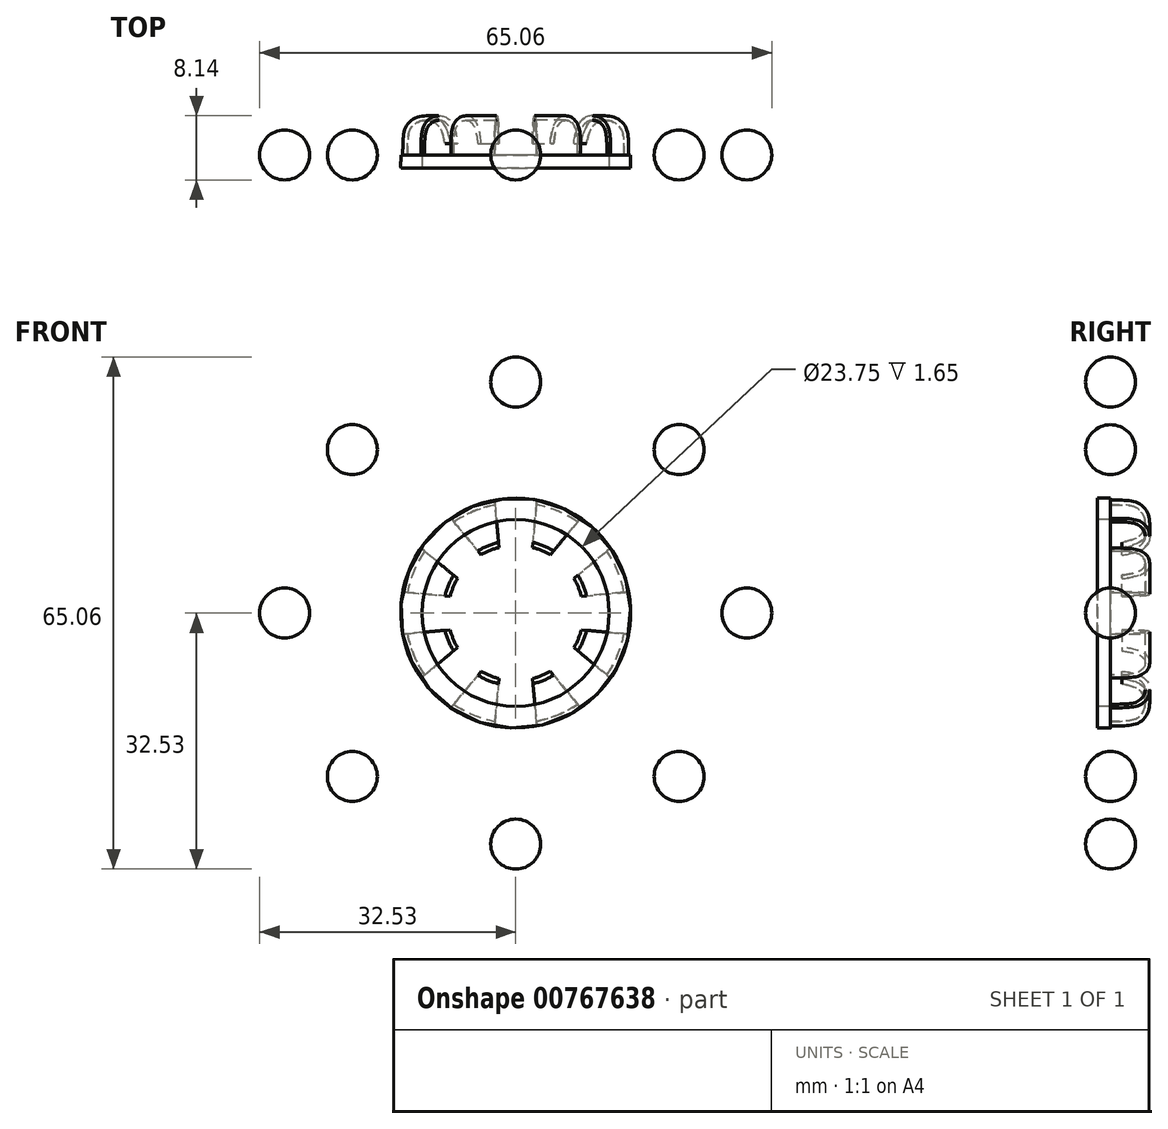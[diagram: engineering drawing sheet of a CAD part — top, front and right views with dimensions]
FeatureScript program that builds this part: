
annotation { "Feature Type Name" : "Feature", "Feature Type Description" : "" }
export const myFeature = defineFeature(function(context is Context, id is Id, definition is map)
    precondition{}
    {
        {
            var Q0;
            Q0=qCreatedBy(makeId("Front.planeOp"),FACE);
            var sketch = newSketch(context, id + "F0", { "sketchPlane" : qUnion([Q0])});
            skCircle(sketch, "E0", {"center": v(0, 0) * mm, "radius": 14.6 * mm});
            skCircle(sketch, "E1", {"center": v(0, 0) * mm, "radius": 11.88 * mm});
            skSolve(sketch);
        }
        {
            var Q0;
            Q0=qCreatedBy(makeId("Front.planeOp"),FACE);
            var sketch = newSketch(context, id + "F1", { "sketchPlane" : qUnion([Q0])});
            skLineSegment(sketch, "E2", {"start": v(0, 0) * mm, "end": v(-49.04, 0) * mm});
            skLineSegment(sketch, "E3", {"start": v(0, 0) * mm, "end": v(-28.37, 28.37) * mm});
            skLineSegment(sketch, "E4", {"start": v(-28.37, 28.37) * mm, "end": v(0, 0) * mm});
            skLineSegment(sketch, "E5", {"start": v(0, 0) * mm, "end": v(0, 0) * mm});
            skLineSegment(sketch, "E6", {"start": v(0, 0) * mm, "end": v(31.83, 31.83) * mm});
            skLineSegment(sketch, "E7", {"start": v(31.83, 31.83) * mm, "end": v(0, 0) * mm});
            skLineSegment(sketch, "E8", {"start": v(0, 0) * mm, "end": v(55.32, 0) * mm});
            skLineSegment(sketch, "E9.MirrorCS", {"start": v(-28.37, -28.37) * mm, "end": v(0, 0) * mm});
            skLineSegment(sketch, "E10.MirrorCS", {"start": v(31.83, -31.83) * mm, "end": v(0, 0) * mm});
            skLineSegment(sketch, "E11", {"start": v(0, 0) * mm, "end": v(0, -25.11) * mm});
            skLineSegment(sketch, "E12", {"start": v(0, -25.11) * mm, "end": v(0, 0) * mm});
            skLineSegment(sketch, "E13", {"start": v(0, 0) * mm, "end": v(-9.1, -21.98) * mm});
            skLineSegment(sketch, "E14", {"start": v(5.91, -1.9) * mm, "end": v(5.91, 1.9) * mm});
            skLineSegment(sketch, "E15", {"start": v(14.8, 2.73) * mm, "end": v(5.91, 1.9) * mm});
            skLineSegment(sketch, "E16", {"start": v(5.91, -1.9) * mm, "end": v(14.8, -2.72) * mm});
            skLineSegment(sketch, "E17", {"start": v(14.8, 2.73) * mm, "end": v(14.8, -2.72) * mm});
            skLineSegment(sketch, "E18.MirrorCS", {"start": v(2.72, 14.8) * mm, "end": v(1.9, 5.91) * mm});
            skLineSegment(sketch, "E19.MirrorCS", {"start": v(-1.9, 5.91) * mm, "end": v(-2.73, 14.8) * mm});
            skLineSegment(sketch, "E20.MirrorCS", {"start": v(2.72, 14.8) * mm, "end": v(-2.73, 14.8) * mm});
            skLineSegment(sketch, "E21.MirrorCS", {"start": v(-1.9, 5.91) * mm, "end": v(1.9, 5.91) * mm});
            skLineSegment(sketch, "E22.MirrorCS", {"start": v(-2.73, -14.8) * mm, "end": v(2.72, -14.8) * mm});
            skLineSegment(sketch, "E23.MirrorCS", {"start": v(-2.73, -14.8) * mm, "end": v(-1.9, -5.91) * mm});
            skLineSegment(sketch, "E24.MirrorCS", {"start": v(1.9, -5.91) * mm, "end": v(-1.9, -5.91) * mm});
            skLineSegment(sketch, "E25.MirrorCS", {"start": v(1.9, -5.91) * mm, "end": v(2.72, -14.8) * mm});
            skLineSegment(sketch, "E26.MirrorCS", {"start": v(-5.91, -1.9) * mm, "end": v(-5.91, 1.9) * mm});
            skLineSegment(sketch, "E27.MirrorCS", {"start": v(-14.8, 2.73) * mm, "end": v(-5.91, 1.9) * mm});
            skLineSegment(sketch, "E28.MirrorCS", {"start": v(-14.8, 2.73) * mm, "end": v(-14.8, -2.72) * mm});
            skLineSegment(sketch, "E29.MirrorCS", {"start": v(-5.91, -1.9) * mm, "end": v(-14.8, -2.72) * mm});
            skLineSegment(sketch, "E30.MirrorCS", {"start": v(-8.54, -12.4) * mm, "end": v(-2.84, -5.53) * mm});
            skLineSegment(sketch, "E31.MirrorCS", {"start": v(-5.53, -2.84) * mm, "end": v(-2.84, -5.53) * mm});
            skLineSegment(sketch, "E32.MirrorCS", {"start": v(-5.53, -2.84) * mm, "end": v(-12.4, -8.54) * mm});
            skLineSegment(sketch, "E33.MirrorCS", {"start": v(-8.54, -12.4) * mm, "end": v(-12.4, -8.54) * mm});
            skLineSegment(sketch, "E34.MirrorCS", {"start": v(2.84, 5.53) * mm, "end": v(5.53, 2.84) * mm});
            skLineSegment(sketch, "E35.MirrorCS", {"start": v(2.84, 5.53) * mm, "end": v(8.54, 12.4) * mm});
            skLineSegment(sketch, "E36.MirrorCS", {"start": v(12.4, 8.54) * mm, "end": v(5.53, 2.84) * mm});
            skLineSegment(sketch, "E37.MirrorCS", {"start": v(12.4, 8.54) * mm, "end": v(8.54, 12.4) * mm});
            skLineSegment(sketch, "E38.MirrorCS", {"start": v(-5.53, 2.84) * mm, "end": v(-2.84, 5.53) * mm});
            skLineSegment(sketch, "E39.MirrorCS", {"start": v(-8.54, 12.4) * mm, "end": v(-2.84, 5.53) * mm});
            skLineSegment(sketch, "E40.MirrorCS", {"start": v(-8.54, 12.4) * mm, "end": v(-12.4, 8.54) * mm});
            skLineSegment(sketch, "E41.MirrorCS", {"start": v(-5.53, 2.84) * mm, "end": v(-12.4, 8.54) * mm});
            skLineSegment(sketch, "E42.MirrorCS", {"start": v(-1.9, -5.91) * mm, "end": v(1.9, -5.91) * mm});
            skLineSegment(sketch, "E43.MirrorCS", {"start": v(-1.9, -5.91) * mm, "end": v(-2.72, -14.8) * mm});
            skLineSegment(sketch, "E44.MirrorCS", {"start": v(2.73, -14.8) * mm, "end": v(-2.72, -14.8) * mm});
            skLineSegment(sketch, "E45.MirrorCS", {"start": v(5.53, -2.84) * mm, "end": v(2.84, -5.53) * mm});
            skLineSegment(sketch, "E46.MirrorCS", {"start": v(5.53, -2.84) * mm, "end": v(12.4, -8.54) * mm});
            skLineSegment(sketch, "E47.MirrorCS", {"start": v(8.54, -12.4) * mm, "end": v(12.4, -8.54) * mm});
            skLineSegment(sketch, "E48.MirrorCS", {"start": v(8.54, -12.4) * mm, "end": v(2.84, -5.53) * mm});
            skSolve(sketch);
        }
        {
            var Q0;
            Q0=qCreatedBy(makeId("Top.planeOp"),FACE);
            var sketch = newSketch(context, id + "F2", { "sketchPlane" : qUnion([Q0])});
            skFitSpline(sketch, "E49", {"points": [v(-14.6, 0) * mm, v(-14.44, 2.84) * mm, v(-13.73, 4.2) * mm, v(-11.98, 4.95) * mm, v(-9.72, 4.28) * mm, v(-8.73, 2.27) * mm, v(-8.6, 1.45) * mm], "startDerivative": vector(0.12, 14.97) * mm, "endDerivative": vector(0, -10.6) * mm});
            skLineSegment(sketch, "E50", {"start": v(-8.6, 1.45) * mm, "end": v(-9.25, 1.45) * mm});
            skFitSpline(sketch, "E51", {"points": [v(-9.25, 1.45) * mm, v(-9.4, 2.07) * mm, v(-10.16, 3.8) * mm, v(-11.97, 4.37) * mm, v(-13.35, 3.69) * mm, v(-13.86, 2.65) * mm, v(-14, 0) * mm], "startDerivative": vector(-1.25, 4.88) * mm, "endDerivative": vector(0, -14.14) * mm});
            skLineSegment(sketch, "E52", {"start": v(0, 0) * mm, "end": v(0, 1.66) * mm});
            skLineSegment(sketch, "E53", {"start": v(-14.6, -1.65) * mm, "end": v(-11.88, -1.65) * mm});
            skLineSegment(sketch, "E54", {"start": v(-14, 0) * mm, "end": v(-11.88, 0) * mm});
            skLineSegment(sketch, "E55", {"start": v(-11.88, 0) * mm, "end": v(-11.88, -1.65) * mm});
            skFitSpline(sketch, "E56", {"points": [v(-14.6, -1.65) * mm, v(-14.6, -0.48) * mm, v(-14.6, 0) * mm], "startDerivative": vector(-0.02, 2.12) * mm, "endDerivative": vector(0.03, 1.15) * mm});
            skSolve(sketch);
        }
        {
            var Q0;
            Q0=makeQuery(id+"F2.imprint","IMPRINT",FACE,{"disambiguationData":[TD([[makeQuery(id+"F2.imprint","IMPRINT",EDGE,{"derivedFrom":sQuery(id+"F2.wireOp",EDGE,"E49")}),-1.0]])]});
            var Q1;
            Q1=makeQuery(id+"F2.imprint","IMPRINT",FACE,{"disambiguationData":[TD([[makeQuery(id+"F2.imprint","IMPRINT",EDGE,{"derivedFrom":sQuery(id+"F2.wireOp",EDGE,"fYS1mkHp-7hg8-m1k1-09gi-qhtqErz1fkrw")}),-1.0]])]});
            var Q2;
            Q2=sQuery(id+"F2.wireOp",EDGE,"E52");
            revolve(context, id + "F3", {"surfaceOperationType" : NewSurfaceOperationType.NEW, "entities" : qUnion([Q0, Q1]), "axis" : qUnion([Q2]), "revolveType" : RevolveType.FULL});
        }
        {
            var Q0;
            Q0 = qSketchRegion(id + "F1", true);
            extrude(context, id + "F4", {"entities" : qUnion([Q0]), "operationType" : NewBodyOperationType.REMOVE, "oppositeDirection" : true, "depth" : 10 * mm, "offsetDistance" : 25 * mm});
        }
        {
            var Q0;
            Q0=qCreatedBy(makeId("Front.planeOp"),FACE);
            var sketch = newSketch(context, id + "F5", { "sketchPlane" : qUnion([Q0])});
            skCircle(sketch, "E57", {"center": v(0, 29.35) * mm, "radius": 3.17 * mm});
            skLineSegment(sketch, "E58", {"start": v(0, 32.53) * mm, "end": v(0, 26.18) * mm});
            skCircle(sketch, "E59.MirrorC", {"center": v(-29.35, 0) * mm, "radius": 3.17 * mm});
            skLineSegment(sketch, "E60.MirrorCS", {"start": v(-32.53, 0) * mm, "end": v(-26.18, 0) * mm});
            skCircle(sketch, "E61.MirrorC", {"center": v(0, -29.35) * mm, "radius": 3.17 * mm});
            skLineSegment(sketch, "E62.MirrorCS", {"start": v(0, -32.53) * mm, "end": v(0, -26.18) * mm});
            skCircle(sketch, "E63.MirrorC", {"center": v(-20.76, -20.76) * mm, "radius": 3.17 * mm});
            skLineSegment(sketch, "E64.MirrorCS", {"start": v(-23, -23) * mm, "end": v(-18.51, -18.51) * mm});
            skCircle(sketch, "E65.MirrorC", {"center": v(20.76, 20.76) * mm, "radius": 3.18 * mm});
            skLineSegment(sketch, "E66.MirrorCS", {"start": v(23, 23) * mm, "end": v(18.51, 18.51) * mm});
            skLineSegment(sketch, "E67.MirrorCS", {"start": v(32.53, 0) * mm, "end": v(26.18, 0) * mm});
            skCircle(sketch, "E68.MirrorC", {"center": v(29.35, 0) * mm, "radius": 3.18 * mm});
            skLineSegment(sketch, "E69.MirrorCS", {"start": v(23, -23) * mm, "end": v(18.51, -18.51) * mm});
            skCircle(sketch, "E70.MirrorC", {"center": v(20.76, -20.76) * mm, "radius": 3.18 * mm});
            skCircle(sketch, "E71.MirrorC", {"center": v(-20.76, 20.76) * mm, "radius": 3.18 * mm});
            skLineSegment(sketch, "E72.MirrorCS", {"start": v(-23, 23) * mm, "end": v(-18.51, 18.51) * mm});
            skSolve(sketch);
        }
        {
            var Q0;
            {var subQ0=sQuery(id+"F5.wireOp",EDGE,"E66.MirrorCS");Q0=makeQuery(id+"F5.imprint","IMPRINT",FACE,{"disambiguationData":[TD([[makeQuery(id+"F5.imprint","IMPRINT",EDGE,{"derivedFrom":subQ0}),-1.0]])]});}
            var Q1;
            Q1=sQuery(id+"F5.wireOp",EDGE,"E66.MirrorCS");
            revolve(context, id + "F6", {"surfaceOperationType" : NewSurfaceOperationType.NEW, "entities" : qUnion([Q0]), "axis" : qUnion([Q1]), "revolveType" : RevolveType.FULL});
        }
        {
            var Q0;
            {var subQ0=sQuery(id+"F5.wireOp",EDGE,"E58");Q0=makeQuery(id+"F5.imprint","IMPRINT",FACE,{"disambiguationData":[TD([[makeQuery(id+"F5.imprint","IMPRINT",EDGE,{"derivedFrom":subQ0}),-1.0]])]});}
            var Q1;
            Q1=sQuery(id+"F5.wireOp",EDGE,"E58");
            revolve(context, id + "F7", {"surfaceOperationType" : NewSurfaceOperationType.NEW, "entities" : qUnion([Q0]), "axis" : qUnion([Q1]), "revolveType" : RevolveType.FULL});
        }
        {
            var Q0;
            {var subQ0=sQuery(id+"F5.wireOp",EDGE,"E72.MirrorCS");Q0=makeQuery(id+"F5.imprint","IMPRINT",FACE,{"disambiguationData":[TD([[makeQuery(id+"F5.imprint","IMPRINT",EDGE,{"derivedFrom":subQ0}),1.0]])]});}
            var Q1;
            Q1=sQuery(id+"F5.wireOp",EDGE,"E72.MirrorCS");
            revolve(context, id + "F8", {"surfaceOperationType" : NewSurfaceOperationType.NEW, "entities" : qUnion([Q0]), "axis" : qUnion([Q1]), "revolveType" : RevolveType.FULL});
        }
        {
            var Q0;
            {var subQ0=sQuery(id+"F5.wireOp",EDGE,"E60.MirrorCS");Q0=makeQuery(id+"F5.imprint","IMPRINT",FACE,{"disambiguationData":[TD([[makeQuery(id+"F5.imprint","IMPRINT",EDGE,{"derivedFrom":subQ0}),1.0]])]});}
            var Q1;
            Q1=sQuery(id+"F5.wireOp",EDGE,"E60.MirrorCS");
            revolve(context, id + "F9", {"surfaceOperationType" : NewSurfaceOperationType.NEW, "entities" : qUnion([Q0]), "axis" : qUnion([Q1]), "revolveType" : RevolveType.FULL});
        }
        {
            var Q0;
            {var subQ0=sQuery(id+"F5.wireOp",EDGE,"E64.MirrorCS");Q0=makeQuery(id+"F5.imprint","IMPRINT",FACE,{"disambiguationData":[TD([[makeQuery(id+"F5.imprint","IMPRINT",EDGE,{"derivedFrom":subQ0}),1.0]])]});}
            var Q1;
            Q1=sQuery(id+"F5.wireOp",EDGE,"E64.MirrorCS");
            revolve(context, id + "F10", {"surfaceOperationType" : NewSurfaceOperationType.NEW, "entities" : qUnion([Q0]), "axis" : qUnion([Q1]), "revolveType" : RevolveType.FULL});
        }
        {
            var Q0;
            {var subQ0=sQuery(id+"F5.wireOp",EDGE,"E62.MirrorCS");Q0=makeQuery(id+"F5.imprint","IMPRINT",FACE,{"disambiguationData":[TD([[makeQuery(id+"F5.imprint","IMPRINT",EDGE,{"derivedFrom":subQ0}),1.0]])]});}
            var Q1;
            Q1=sQuery(id+"F5.wireOp",EDGE,"E62.MirrorCS");
            revolve(context, id + "F11", {"surfaceOperationType" : NewSurfaceOperationType.NEW, "entities" : qUnion([Q0]), "axis" : qUnion([Q1]), "revolveType" : RevolveType.FULL});
        }
        {
            var Q0;
            {var subQ0=sQuery(id+"F5.wireOp",EDGE,"E67.MirrorCS");Q0=makeQuery(id+"F5.imprint","IMPRINT",FACE,{"disambiguationData":[TD([[makeQuery(id+"F5.imprint","IMPRINT",EDGE,{"derivedFrom":subQ0}),-1.0]])]});}
            var Q1;
            Q1=sQuery(id+"F5.wireOp",EDGE,"E67.MirrorCS");
            revolve(context, id + "F12", {"surfaceOperationType" : NewSurfaceOperationType.NEW, "entities" : qUnion([Q0]), "axis" : qUnion([Q1]), "revolveType" : RevolveType.FULL});
        }
        {
            var Q0;
            {var subQ0=sQuery(id+"F5.wireOp",EDGE,"E69.MirrorCS");Q0=makeQuery(id+"F5.imprint","IMPRINT",FACE,{"disambiguationData":[TD([[makeQuery(id+"F5.imprint","IMPRINT",EDGE,{"derivedFrom":subQ0}),1.0]])]});}
            var Q1;
            Q1=sQuery(id+"F5.wireOp",EDGE,"E69.MirrorCS");
            revolve(context, id + "F13", {"surfaceOperationType" : NewSurfaceOperationType.NEW, "entities" : qUnion([Q0]), "axis" : qUnion([Q1]), "revolveType" : RevolveType.FULL});
        }
    });
